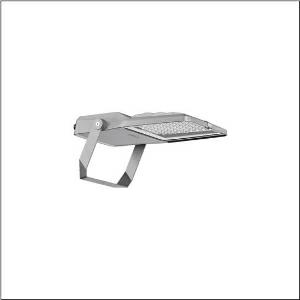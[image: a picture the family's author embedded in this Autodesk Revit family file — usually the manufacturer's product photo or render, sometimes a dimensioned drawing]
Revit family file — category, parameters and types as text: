
# Revit family: floodlight_fl_21_iq_mini___pl33t_5xa7772c4f1a_48c1
name_source: partatom
category: Lighting Fixtures
units: mm (PartAtom-declared; Revit-internal decimal feet)

## family parameters
Cut with Voids When Loaded = No
Host = Face
Light Source = No
Part Type = Normal
Room Calculation Point = No
Round Connector Dimension = Use Diameter
Shared = No

## types (1)
- --- (1 x LED, 12570 lm, 87.2 W, 4000K)
    Apparent Load = 87 VA
    CIE Flux Codes = 26 75 99 100 100
    Color Rendering = 70
    Color Temperature = 4000K
    Default Elevation = 1800 mm
    Description = Floodlight FL 21 iQ mini, floodlight, primary light control with lens, of PMMA, primary optical cover: protective disc, of toughened safety glass, transparent, light distribution: PL33T, light emission: direct distribution, installation type: surface-mounted, LED, High Power LED, rated luminous flux: 12.570lm, luminous efficacy: 144lm/W, light colour: 740, colour temperature: 4000K, control gear: iQ Street-Remote/DALI, control: Street-Remote, Auto-Match, Temp-Guard, Night-Set, Smart-Wire, Desk-Remote (wireless, voltage-free reading and setting of iQ features in the workshop via application-optimized NFC function/RFID function), optimised constant luminous flux control (CLO 2.0), with terminal, 6-pole, mains connection: 220..240V, AC, 50/60Hz, start of lifetime: 87W, end of service life: 92W, reduction: 40W, luminaire housing, of diecast aluminium, powder-coated, Siteco® metallic grey (DB 702S), corrosivity category C5 mid according to DIN EN ISO 12944, suitable for swimming pools, chlorine-resistant, sealing non-destructively replaceable, mounting bracket, of steel, galvanised, powder-coated, Siteco® metallic grey (DB 702S), protection rating (complete): IP66, insulation class (complete): insulation class II (safety insulation), certification: CE, ENEC, VDE, protection symbol: D, impact resistance: IK08, permissible operating ambient temperature: -40..+40°C, permissible operating ambient temperature for outdoor applications: -40..+50°C, standard: DIN EN 12944, LABS conformity tested according to VDMA 24364:2018-05, packaging unit: 1 piece

Light Distribution: PL33T
    Height = 70 mm
    Lamp = 1 x LED
    Lamp Light Flux = 12570 lm
    Lamp Power = 87.2 W
    Lamp count = 1
    Length = 485 mm
    Luminous efficacy = 144 lm/W
    Manufacturer = Siteco
    ModVariant = No
    Model = 5XA7772C4F1A
    Number of Poles = 1
    OnlyDefault = Yes
    Power Factor = 1
    Product Name = Floodlight FL 21 iQ mini | PL33T
    Product group = floodlight | pylon annexe
    ProductGroupID = 6200
    Protection Class = Protection class II
    Protection Degree = IP 66
    RLX_Detail_Level = 1
    RLX_Emergency_Light_Flux = 0 lm
    RLX_Emergency_Type = 0
    RLX_Emergency_Type_DB = No
    RlxData = <blob elided: 96317 chars, md5=ee399126>
    Socket = socket
    Standby Power = 0 W
    System Light Flux = 12570 lm
    System Power = 87 W
    Type Comments = factory setting: luminous flux: 100 % | dim-lin: 254 | 456 mA
    Type Image = l_1006845.jpg
    URL = http://relux.com
    VarID = @adj_149420
    Voltage = 0 V
    Weight = 0.00 kg
    Width = 337 mm

## geometry (parser evidence)
native form markers: Blend x4, Sweep x14
no freeform markers — native parametric forms only
